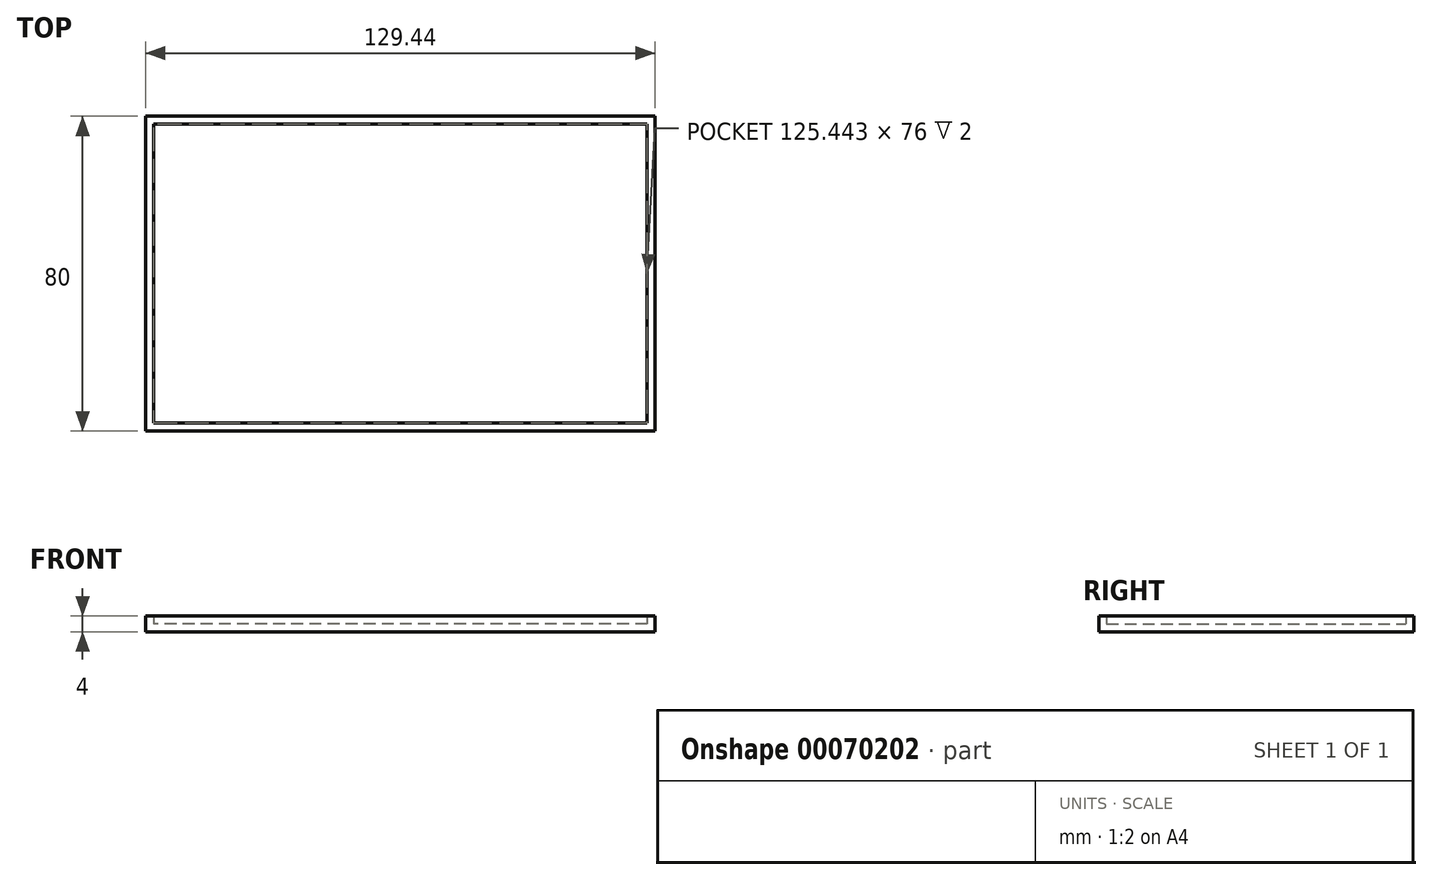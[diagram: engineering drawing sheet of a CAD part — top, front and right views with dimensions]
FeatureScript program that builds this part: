
annotation { "Feature Type Name" : "Feature", "Feature Type Description" : "" }
export const myFeature = defineFeature(function(context is Context, id is Id, definition is map)
    precondition{}
    {
        {
            var Q0;
            Q0=qCreatedBy(makeId("Top.planeOp"),FACE);
            var sketch = newSketch(context, id + "F0", { "sketchPlane" : qUnion([Q0])});
            skLineSegment(sketch, "E0.rect.bottom", {"start": v(-64.72, 40) * mm, "end": v(64.72, 40) * mm});
            skLineSegment(sketch, "E0.rect.top", {"start": v(-64.72, -40) * mm, "end": v(64.72, -40) * mm});
            skLineSegment(sketch, "E0.rect.left", {"start": v(-64.72, 40) * mm, "end": v(-64.72, -40) * mm});
            skLineSegment(sketch, "E0.rect.right", {"start": v(64.72, 40) * mm, "end": v(64.72, -40) * mm});
            skPoint(sketch, "E0.rect.middle", {"position": v(0, 0) * mm});
            skSolve(sketch);
        }
        {
            var Q0;
            Q0 = qSketchRegion(id + "F0", true);
            extrude(context, id + "F1", {"entities" : qUnion([Q0]), "oppositeDirection" : true, "depth" : 2 * mm});
        }
        {
            var Q0;
            Q0=qCreatedBy(makeId("Top.planeOp"),FACE);
            var sketch = newSketch(context, id + "F2", { "sketchPlane" : qUnion([Q0])});
            skLineSegment(sketch, "E1.bottom", {"start": v(-64.72, 40) * mm, "end": v(64.72, 40) * mm});
            skLineSegment(sketch, "E1.top", {"start": v(-64.72, -40) * mm, "end": v(64.72, -40) * mm});
            skLineSegment(sketch, "E1.left", {"start": v(-64.72, 40) * mm, "end": v(-64.72, -40) * mm});
            skLineSegment(sketch, "E1.right", {"start": v(64.72, 40) * mm, "end": v(64.72, -40) * mm});
            skLineSegment(sketch, "E2.0", {"start": v(62.72, 38) * mm, "end": v(-62.72, 38) * mm});
            skLineSegment(sketch, "E2.1", {"start": v(62.72, -38) * mm, "end": v(62.72, 38) * mm});
            skLineSegment(sketch, "E2.2", {"start": v(-62.72, -38) * mm, "end": v(62.72, -38) * mm});
            skLineSegment(sketch, "E2.3", {"start": v(-62.72, 38) * mm, "end": v(-62.72, -38) * mm});
            skSolve(sketch);
        }
        {
            var Q0;
            Q0 = qSketchRegion(id + "F2", true);
            extrude(context, id + "F3", {"entities" : qUnion([Q0]), "operationType" : NewBodyOperationType.ADD, "depth" : 2 * mm});
        }
    });
